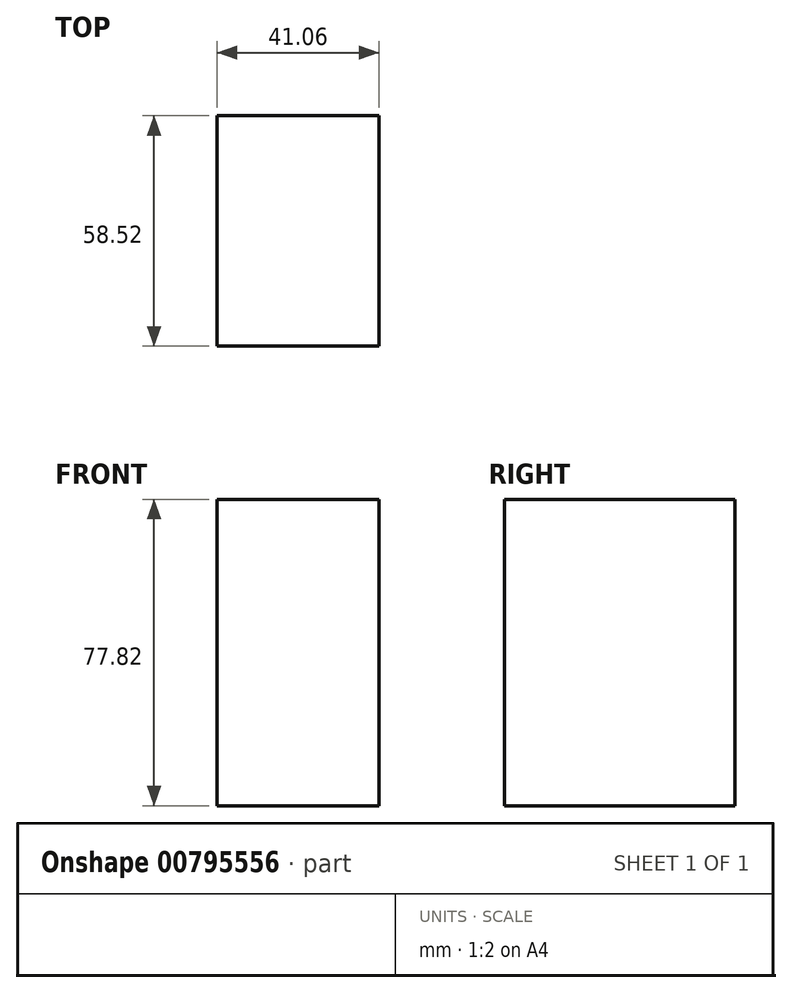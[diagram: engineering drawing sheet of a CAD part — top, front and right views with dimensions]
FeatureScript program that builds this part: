
annotation { "Feature Type Name" : "Feature", "Feature Type Description" : "" }
export const myFeature = defineFeature(function(context is Context, id is Id, definition is map)
    precondition{}
    {
        {
            var Q0;
            Q0=qCreatedBy(makeId("Top.planeOp"),FACE);
            var sketch = newSketch(context, id + "F0", { "sketchPlane" : qUnion([Q0])});
            skLineSegment(sketch, "E0.bottom", {"start": v(-23.7, 27.13) * mm, "end": v(17.35, 27.13) * mm});
            skLineSegment(sketch, "E0.top", {"start": v(-23.7, -31.4) * mm, "end": v(17.35, -31.4) * mm});
            skLineSegment(sketch, "E0.left", {"start": v(-23.7, 27.13) * mm, "end": v(-23.7, -31.4) * mm});
            skLineSegment(sketch, "E0.right", {"start": v(17.35, 27.13) * mm, "end": v(17.35, -31.4) * mm});
            skSolve(sketch);
        }
        {
            var Q0;
            Q0=makeQuery(id+"F0.imprint","IMPRINT",FACE,{"disambiguationData":[TD([[makeQuery(id+"F0.imprint","IMPRINT",EDGE,{"derivedFrom":sQuery(id+"F0.wireOp",EDGE,"E0.bottom")}),-1.0]])]});
            extrude(context, id + "F1", {"entities" : qUnion([Q0]), "depth" : 77.82 * mm, "offsetDistance" : 25.4 * mm});
        }
    });
